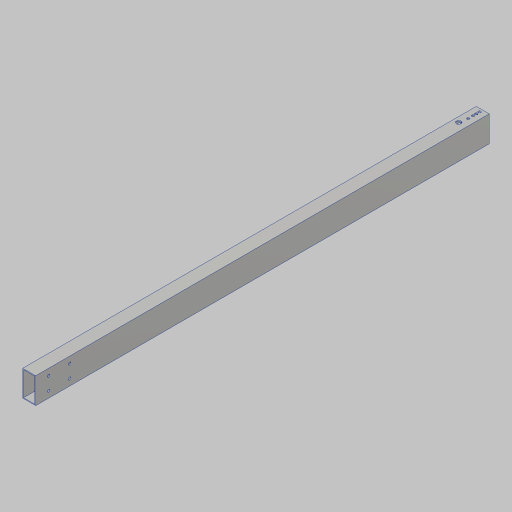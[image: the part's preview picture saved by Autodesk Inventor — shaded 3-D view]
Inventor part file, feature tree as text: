
AUTODESK INVENTOR PART (.ipt)
format: ipt  version: 2023.5 (Build 275446000, 446)  size: 312,320 bytes
history: native  units: in
note: dims shown in document units (in); Inventor stores cm internally (conversion verified against a paired STEP export)
features: sketch x4, hole x3, extrude x2, fillet x1, projected_geometry x1
ambient origin geometry x8: Origin, YZ Plane, XZ Plane, XY Plane, X Axis, Y Axis, Z Axis, Center Point
bodies: Solid1 (feature_tree)
feature tree (11):
  extrude  "Extrusion1"  Depth=0.5in
  hole  "Hole1"  [1 undecoded]
  hole  "Hole3"  [1 undecoded]
  extrude  "Extrusion2"  Depth=1.0in
  fillet  "Fillet1"  Radius=1.0in
  hole  "Hole4"  [1 undecoded]
  sketch  "Sketch2"  dims[d4=0.0in d5=0.5in]
  sketch  "Sketch4"  dims[d6=0.25in d7=0.25in]
  sketch  "Sketch5"  dims[d8=0.25in]
  sketch  "Sketch6"  dims[d9=0.201in d10=0.75in d11=0.385in d12=0.25in d13=0.5635in d14=1.0in d15=0.8108in d27=0.812in d28=0.391in d29=1.0in d30=0.375in d31=0.75in d32=0.385in d33=0.25in d34=0.5635in d35=1.0in d36=0.8108in d37=1.1in d38=1.25in d41=0.0625in d42=0.0in d43=1.75in d44=0.13in d45=0.375in d46=1.0in d47=0.5in d48=0.5in d49=1.625in d50=0.201in d51=0.75in d52=0.385in d53=0.25in d54=0.5635in d55=1.0in d56=0.8108in]
  projected_geometry  "Projected Loop1"
note: 3 required parameter values undecoded (feature->parameter linkage not recoverable at this tier; creation-order binding heuristic only, values carry confidence <= 0.55)
